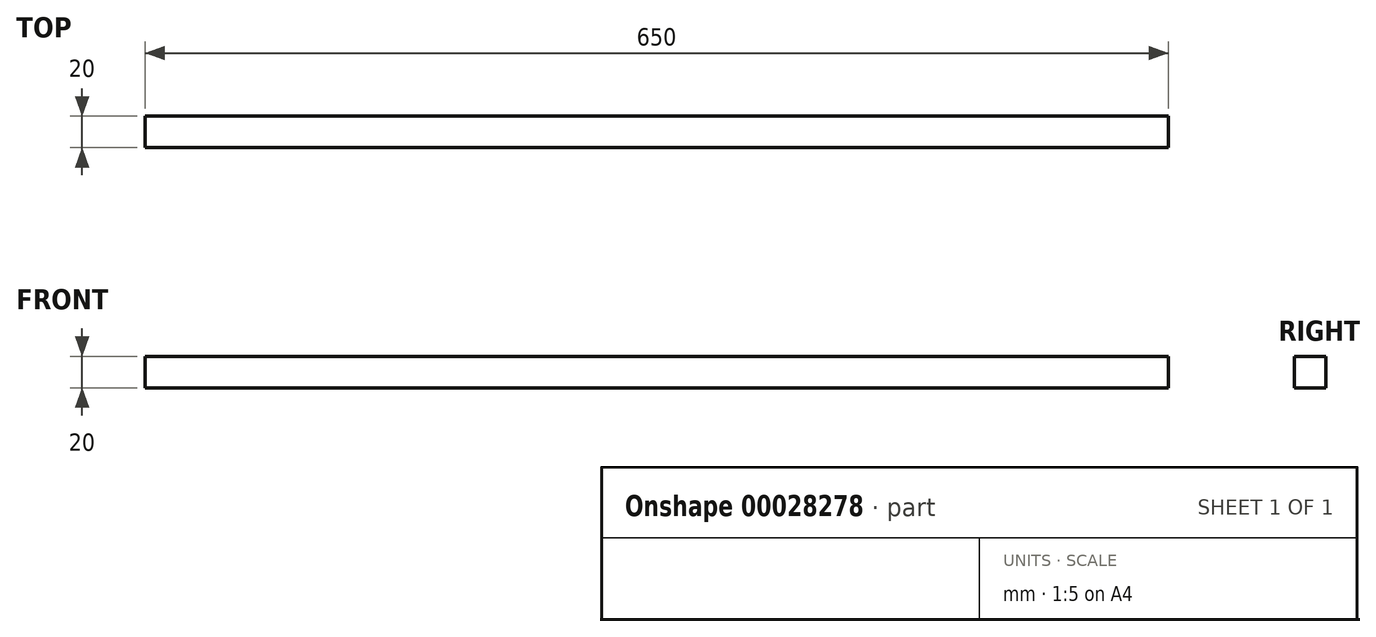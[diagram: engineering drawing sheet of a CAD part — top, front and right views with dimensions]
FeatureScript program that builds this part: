
annotation { "Feature Type Name" : "Feature", "Feature Type Description" : "" }
export const myFeature = defineFeature(function(context is Context, id is Id, definition is map)
    precondition{}
    {
        {
            var Q0;
            Q0=qCreatedBy(makeId("Top.planeOp"),FACE);
            var sketch = newSketch(context, id + "F0", { "sketchPlane" : qUnion([Q0])});
            skLineSegment(sketch, "E0.bottom", {"start": v(0, 0) * mm, "end": v(650, 0) * mm});
            skLineSegment(sketch, "E0.top", {"start": v(0, 20) * mm, "end": v(650, 20) * mm});
            skLineSegment(sketch, "E0.left", {"start": v(0, 0) * mm, "end": v(0, 20) * mm});
            skLineSegment(sketch, "E0.right", {"start": v(650, 0) * mm, "end": v(650, 20) * mm});
            skSolve(sketch);
        }
        {
            var Q0;
            Q0=makeQuery(id+"F0.imprint","IMPRINT",FACE,{"disambiguationData":[TD([[makeQuery(id+"F0.imprint","IMPRINT",EDGE,{"derivedFrom":sQuery(id+"F0.wireOp",EDGE,"E0.bottom")}),1.0]])]});
            extrude(context, id + "F1", {"entities" : qUnion([Q0]), "depth" : 20 * mm});
        }
    });
